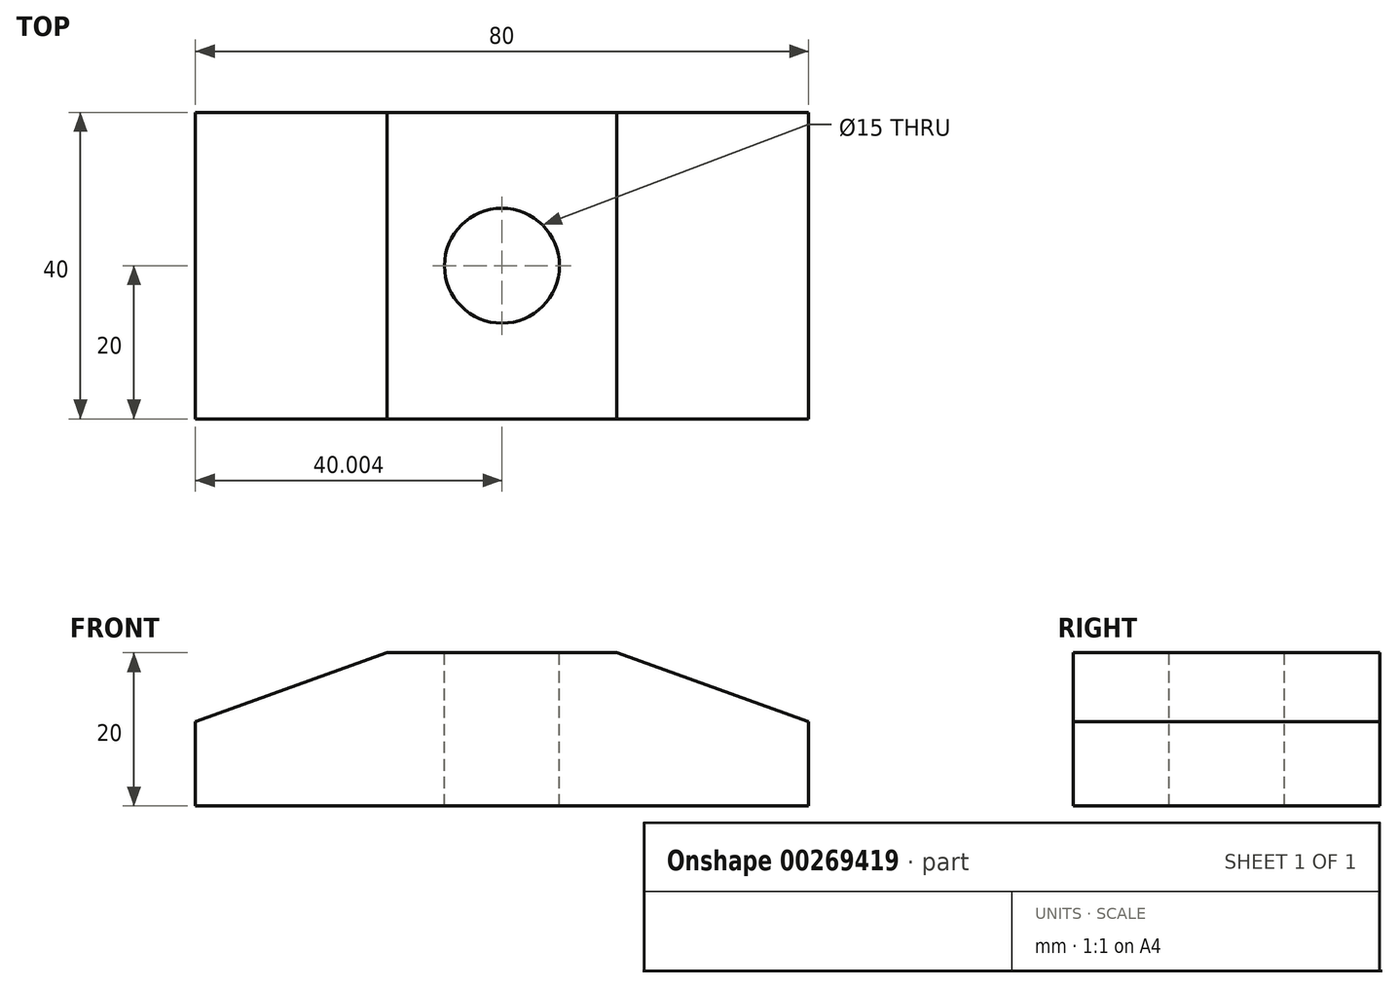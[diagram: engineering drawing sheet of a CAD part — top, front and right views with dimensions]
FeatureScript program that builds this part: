
annotation { "Feature Type Name" : "Feature", "Feature Type Description" : "" }
export const myFeature = defineFeature(function(context is Context, id is Id, definition is map)
    precondition{}
    {
        {
            var Q0;
            Q0=qCreatedBy(makeId("Front.planeOp"),FACE);
            var sketch = newSketch(context, id + "F0", { "sketchPlane" : qUnion([Q0])});
            skLineSegment(sketch, "E0", {"start": v(-54.04, -44.65) * mm, "end": v(25.96, -44.65) * mm});
            skLineSegment(sketch, "E1", {"start": v(25.96, -44.65) * mm, "end": v(25.96, -33.65) * mm});
            skLineSegment(sketch, "E2", {"start": v(25.96, -33.65) * mm, "end": v(0.96, -24.65) * mm});
            skLineSegment(sketch, "E3", {"start": v(0.96, -24.65) * mm, "end": v(-29.04, -24.65) * mm});
            skLineSegment(sketch, "E4", {"start": v(-29.04, -24.65) * mm, "end": v(-54.04, -33.65) * mm});
            skLineSegment(sketch, "E5", {"start": v(-54.04, -33.65) * mm, "end": v(-54.04, -44.65) * mm});
            skSolve(sketch);
        }
        {
            var Q0;
            Q0=makeQuery(id+"F0.imprint","IMPRINT",FACE,{"disambiguationData":[TD([[makeQuery(id+"F0.imprint","IMPRINT",EDGE,{"derivedFrom":sQuery(id+"F0.wireOp",EDGE,"E0")}),1.0]])]});
            extrude(context, id + "F1", {"entities" : qUnion([Q0]), "depth" : 40 * mm});
        }
        {
            var Q0;
            Q0=makeQuery(id+"F1.opExtrude","SWEPT_FACE",FACE,{"disambiguationData":[OSD([sQuery(id+"F0.wireOp",EDGE,"E3")])]});
            var sketch = newSketch(context, id + "F2", { "sketchPlane" : qUnion([Q0])});
            skCircle(sketch, "E6", {"center": v(-14.04, -20) * mm, "radius": 7.5 * mm});
            skPoint(sketch, "E6.centerSnap0", {"position": v(0.96, -20) * mm});
            skPoint(sketch, "E6.centerSnap1", {"position": v(-14.04, -40) * mm});
            skSolve(sketch);
        }
        {
            var Q0;
            Q0=makeQuery(id+"F2.imprint","IMPRINT",FACE,{"disambiguationData":[TD([[makeQuery(id+"F2.imprint","IMPRINT",EDGE,{"derivedFrom":sQuery(id+"F2.wireOp",EDGE,"E6")}),1.0]])]});
            extrude(context, id + "F3", {"entities" : qUnion([Q0]), "operationType" : NewBodyOperationType.REMOVE, "oppositeDirection" : true, "depth" : 53.85 * mm});
        }
    });
